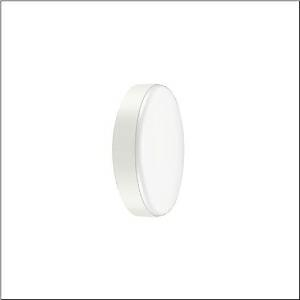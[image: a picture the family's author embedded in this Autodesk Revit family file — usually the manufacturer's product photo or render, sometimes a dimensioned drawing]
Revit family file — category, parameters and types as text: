
# Revit family: round_31_51wc10ma42as
name_source: partatom
category: Lighting Fixtures
units: mm (PartAtom-declared; Revit-internal decimal feet)

## family parameters
Cut with Voids When Loaded = No
Host = Face
Light Source = No
Part Type = Normal
Room Calculation Point = No
Round Connector Dimension = Use Diameter
Shared = No

## types (1)
- --- (1 x LED, 2550 lm, 20.5 W, 4000K)
    Apparent Load = 21 VA
    CIE Flux Codes = 44 75 94 94 100
    Color Rendering = 80
    Color Temperature = 4000K
    Default Elevation = 1800 mm
    Description = Round 31, wall and ceiling luminaire, primary optical cover: cover, of PC, opal, light emission: direct distribution, primary light characteristic: symmetric, installation type: surface-mounted, LED, rated luminous flux: 2.550lm, luminous efficacy: 124lm/W, light colour: 840, colour temperature: 4000K, control gear: ON/OFF Multilumen, with terminal, 3-pole, max. 2.5mm², mains connection: 220..240V, AC, 50/60Hz, rated input power: 20.5W, luminaire housing, of PC, traffic white (RAL 9016), diameter: 350mm, brightness and presence sensor, HF sensor, protection rating (complete): IP65, insulation class (complete): insulation class II (safety insulation), certification: CE, impact resistance: IK10, permissible operating ambient temperature: -20..+40°C, permissible storage temperature: -20..+60°C, packaging unit: 1 piece
    Height = 97 mm
    Lamp = 1 x LED
    Lamp Light Flux = 2550 lm
    Lamp Power = 20.5 W
    Lamp count = 1
    Length = 350 mm
    Luminous efficacy = 124 lm/W
    Manufacturer = Siteco
    ModVariant = No
    Model = 51WC10MA42AS
    Mounting Place = Wall
    Mounting Type = Surface mounted
    Number of Poles = 1
    OnlyDefault = Yes
    Power Factor = 1
    Product Name = Round 31
    Product group = wall and ceiling luminaire | wall mounted
    ProductGroupID = 2001
    Protection Class = Protection class II
    Protection Degree = IP 65
    RLX_Detail_Level = 1
    RLX_Emergency_Light_Flux = 0 lm
    RLX_Emergency_Type = 0
    RLX_Emergency_Type_DB = No
    RlxData = <blob elided: 30457 chars, md5=f2d365fa>
    Socket = socket
    Standby Power = 0 W
    System Light Flux = 2550 lm
    System Power = 21 W
    Type Comments = factory setting: luminous flux: 100 % | (ON | ON)
    Type Image = l_1007027.jpg
    URL = http://relux.com
    VarID = @adj_150309
    Voltage = 0 V
    Weight = 0.00 kg
    Width = 0 mm  [stored 0 ft]

note: [stored X ft] marks values corroborated as IEEE doubles in the binary element streams (Revit-internal decimal feet)

## geometry (parser evidence)
native form markers: Blend x4, Sweep x12
no freeform markers — native parametric forms only
